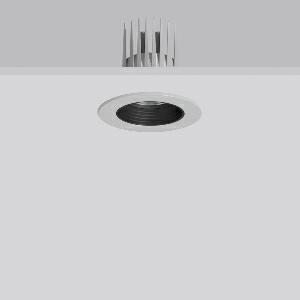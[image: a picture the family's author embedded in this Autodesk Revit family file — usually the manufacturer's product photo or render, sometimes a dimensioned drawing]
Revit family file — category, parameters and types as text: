
# Revit family: heledon_mini_e_901755_004_1_76_14d3
name_source: partatom
category: Lighting Fixtures
units: mm (PartAtom-declared; Revit-internal decimal feet)

## family parameters
Cut with Voids When Loaded = No
Host = Face
Light Source = No
Part Type = Normal
Room Calculation Point = No
Round Connector Dimension = Use Diameter
Shared = No

## types (1)
- HELEDON mini E (1 x LED Modul 940, 2950 lm, 4000)
    Apparent Load = 29 VA
    Approval mark = CE
    CIE Flux Codes = 95 100 100 100 100
    Color Rendering = 92
    Color Temperature = 4000
    Default Elevation = 1800 mm
    Description = Series: HELEDON mini
Round recessed downlight. Housing: die-cast aluminium, powder-coated. Black plastic ring and recessed LED to prevent glare from the side. Optical assembly with lens made of plastic (polycarbonate) for the best homogeneous light distribution - can be changed without tools. Best colour rendering index Ra>90. Suitable for Recessed ceiling mounting. Installation without tools thanks to spring fastening system. Including separate LED converter with connecting cable 600 mm.High quality converter without flickering and stroboscopic effect. Through-wiring box (5 pole) available as accessory. The following accessories can be mounted without use of tools: interchangeable lenses, decorative glasses, honeycomb louvre, clear and frosted diffusers, white interchangeable plastic ring. 
Colour: silver
Diameter: 124 mm
Height: 3 mm
Cut-out diameter: 114 mm
Recess height: 170 mm
Luminaire: recess height: 120 mm
Lamp: LED
Socket: without socket
Colour temperature: 4000K
Colour rendering index (CRI): 92
System power: 29 W
Rated luminous flux: 2950 lm
Luminous efficiency: 102 lm/W
Control gear: Converter, dimmable, DALI
Protection class: II
Type of protection: IP 20
    Height = 0 mm  [stored 0 ft]
    Lamp = 1 x LED Modul 940
    Lamp Light Flux = 2950 lm
    Lamp count = 1
    Length = 124 mm  [stored 0.406824 ft]
    Lifetime = 50000 h
    Luminous efficacy = 102 lm/W
    Manufacturer = RZB
    ModVariant = No
    Model = 901755.004.1.76
    Mounting Place = Ceiling
    Mounting Type = Recessed
    Number of Poles = 1
    OnlyDefault = Yes
    Power Factor = 1
    Product Name = HELEDON mini E
    Product group = Recessed downlights
    ProductGroupID = 402
    Protection Class = Protection class II
    Protection Degree = IP 20
    RLX_Detail_Level = 1
    RLX_Emergency_Light_Flux = 0 lm
    RLX_Emergency_Type = 0
    RLX_Emergency_Type_DB = No
    RlxData = <blob elided: 134217 chars, md5=fc960437>
    Socket = socket
    Standby Power = 0 W
    System Light Flux = 2950 lm
    System Power = 29 W
    Type Comments = Product without accessories
    Type Image = 901656.004.jpg
    URL = http://relux.com
    VarID = ---
    Voltage = 230 V
    Voltage Range = 220-240 V
    Weight = 0.00 kg
    Width = 0 mm  [stored 0 ft]

note: [stored X ft] marks values corroborated as IEEE doubles in the binary element streams (Revit-internal decimal feet)

## geometry (parser evidence)
native form markers: Blend x4, Sweep x10
no freeform markers — native parametric forms only
